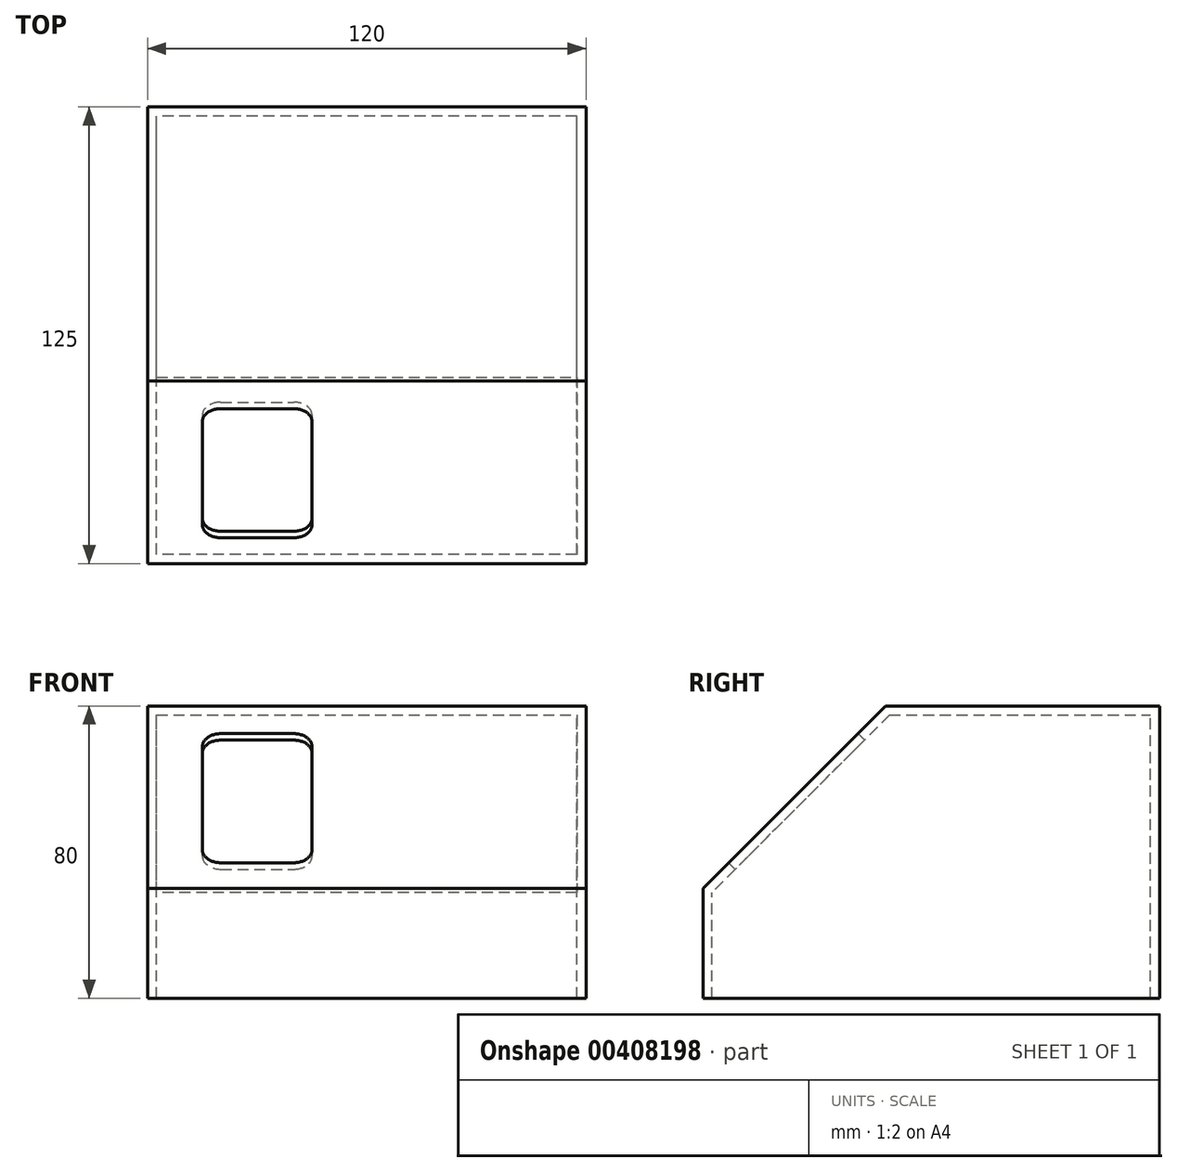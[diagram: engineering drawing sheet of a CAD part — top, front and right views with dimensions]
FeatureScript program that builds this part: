
annotation { "Feature Type Name" : "Feature", "Feature Type Description" : "" }
export const myFeature = defineFeature(function(context is Context, id is Id, definition is map)
    precondition{}
    {
        {
            var Q0;
            Q0=qCreatedBy(makeId("Front.planeOp"),FACE);
            var sketch = newSketch(context, id + "F0", { "sketchPlane" : qUnion([Q0])});
            skLineSegment(sketch, "E0.bottom", {"start": v(0, 0) * mm, "end": v(-120, 0) * mm});
            skLineSegment(sketch, "E0.top", {"start": v(0, 80) * mm, "end": v(-120, 80) * mm});
            skLineSegment(sketch, "E0.left", {"start": v(0, 0) * mm, "end": v(0, 80) * mm});
            skLineSegment(sketch, "E0.right", {"start": v(-120, 0) * mm, "end": v(-120, 80) * mm});
            skSolve(sketch);
        }
        {
            var Q0;
            Q0=makeQuery(id+"F0.imprint","IMPRINT",FACE,{"disambiguationData":[TD([[makeQuery(id+"F0.imprint","IMPRINT",EDGE,{"derivedFrom":sQuery(id+"F0.wireOp",EDGE,"E0.bottom")}),-1.0]])]});
            extrude(context, id + "F1", {"entities" : qUnion([Q0]), "endBound" : BoundingType.SYMMETRIC, "depth" : 125 * mm});
        }
        {
            var Q0;
            Q0=makeQuery(id+"F1.opExtrude","CAP_EDGE",EDGE,{"disambiguationData":[OSD([sQuery(id+"F0.wireOp",EDGE,"E0.top")])],"isStart":false});
            chamfer(context, id + "F2", {"entities" : qUnion([Q0]), "width" : 50 * mm, "tangentPropagation" : true});
        }
        {
            var Q0;
            Q0=makeQuery(id+"F1.opExtrude","SWEPT_FACE",FACE,{"disambiguationData":[OSD([sQuery(id+"F0.wireOp",EDGE,"E0.bottom")])]});
            shell(context, id + "F3", {"entities" : qUnion([Q0]), "thickness" : 2.5 * mm});
        }
        {
            var Q0;
            Q0=makeQuery(id+"F2.opChamfer","BLEND_FACE",FACE,{"disambiguationData":[OSD([sQuery(id+"F0.wireOp",EDGE,"E0.top")])]});
            var sketch = newSketch(context, id + "F4", { "sketchPlane" : qUnion([Q0])});
            skLineSegment(sketch, "E1.bottom", {"start": v(-100, 37.02) * mm, "end": v(-80, 37.02) * mm});
            skLineSegment(sketch, "E1.top", {"start": v(-100, -12.98) * mm, "end": v(-80, -12.98) * mm});
            skLineSegment(sketch, "E1.left", {"start": v(-105, 32.02) * mm, "end": v(-105, -7.98) * mm});
            skLineSegment(sketch, "E1.right", {"start": v(-75, 32.02) * mm, "end": v(-75, -7.98) * mm});
            skPoint(sketch, "E2.visualSharp", {"position": v(-105, 37.02) * mm});
            skArc(sketch, "E2.filletArc", {"start": v(-100, 37.02) * mm, "mid": v(-103.54, 35.55) * mm, "end": v(-105, 32.02) * mm});
            skPoint(sketch, "E3.visualSharp", {"position": v(-75, 37.02) * mm});
            skArc(sketch, "E3.filletArc", {"start": v(-75, 32.02) * mm, "mid": v(-76.46, 35.55) * mm, "end": v(-80, 37.02) * mm});
            skPoint(sketch, "E4.visualSharp", {"position": v(-75, -12.98) * mm});
            skArc(sketch, "E4.filletArc", {"start": v(-80, -12.98) * mm, "mid": v(-76.46, -11.52) * mm, "end": v(-75, -7.98) * mm});
            skPoint(sketch, "E5.visualSharp", {"position": v(-105, -12.98) * mm});
            skArc(sketch, "E5.filletArc", {"start": v(-105, -7.98) * mm, "mid": v(-103.54, -11.52) * mm, "end": v(-100, -12.98) * mm});
            skSolve(sketch);
        }
        {
            var Q0;
            Q0=makeQuery(id+"F4.imprint","IMPRINT",FACE,{"disambiguationData":[TD([[makeQuery(id+"F4.imprint","IMPRINT",EDGE,{"derivedFrom":sQuery(id+"F4.wireOp",EDGE,"E1.bottom")}),-1.0]])]});
            extrude(context, id + "F5", {"entities" : qUnion([Q0]), "operationType" : NewBodyOperationType.REMOVE, "oppositeDirection" : true, "depth" : 25 * mm});
        }
    });
